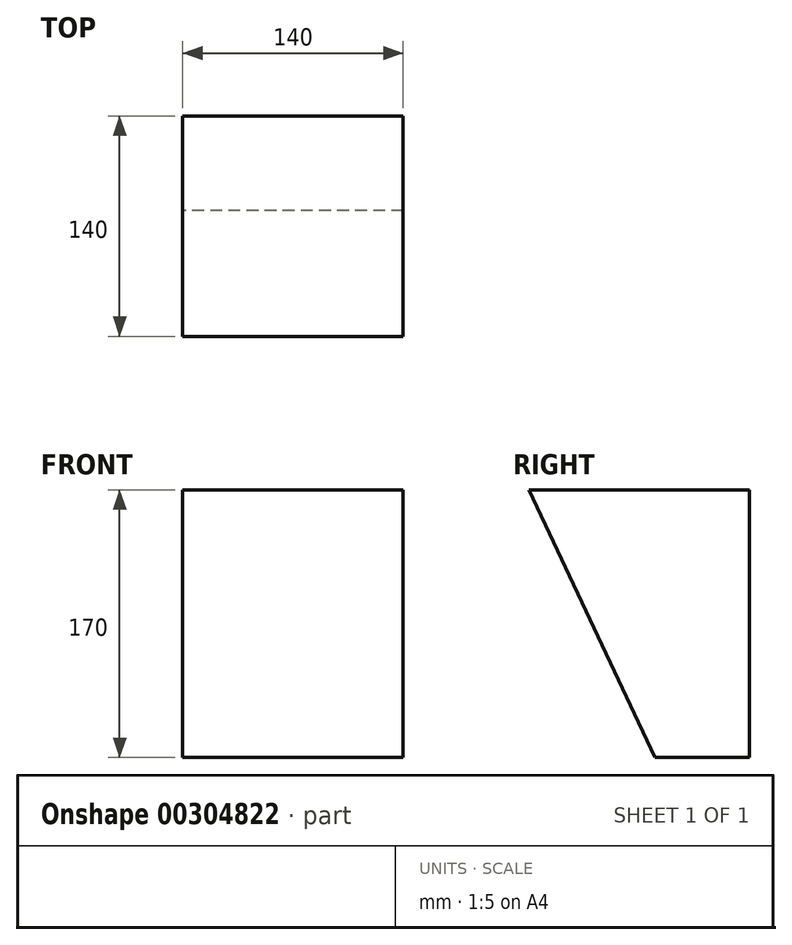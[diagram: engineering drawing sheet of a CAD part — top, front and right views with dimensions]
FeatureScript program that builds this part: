
annotation { "Feature Type Name" : "Feature", "Feature Type Description" : "" }
export const myFeature = defineFeature(function(context is Context, id is Id, definition is map)
    precondition{}
    {
        {
            var Q0;
            Q0=qCreatedBy(makeId("Top.planeOp"),FACE);
            cPlane(context, id + "F0", {"entities" : qUnion([Q0]), "cplaneType" : CPlaneType.OFFSET, "offset" : 170 * mm, "width" : 150 * mm, "height" : 150 * mm});
        }
        {
            var Q0;
            Q0=qCreatedBy(id+"F0.planeOp",FACE);
            var sketch = newSketch(context, id + "F1", { "sketchPlane" : qUnion([Q0])});
            skLineSegment(sketch, "E0.bottom", {"start": v(70, -140) * mm, "end": v(-70, -140) * mm});
            skLineSegment(sketch, "E0.top", {"start": v(70, 0) * mm, "end": v(-70, 0) * mm});
            skLineSegment(sketch, "E0.left", {"start": v(70, -140) * mm, "end": v(70, 0) * mm});
            skLineSegment(sketch, "E0.right", {"start": v(-70, -140) * mm, "end": v(-70, 0) * mm});
            skPoint(sketch, "E0.middle", {"position": v(0, 0) * mm});
            skSolve(sketch);
        }
        {
            var Q0;
            Q0=qCreatedBy(makeId("Top.planeOp"),FACE);
            var sketch = newSketch(context, id + "F2", { "sketchPlane" : qUnion([Q0])});
            skPoint(sketch, "E1", {"position": v(-340, 140) * mm});
            skPoint(sketch, "E2", {"position": v(-340, -140) * mm});
            skPoint(sketch, "E3", {"position": v(0, -60) * mm});
            skPoint(sketch, "E4", {"position": v(0, 60) * mm});
            skLineSegment(sketch, "E5", {"start": v(-340, 140) * mm, "end": v(-340, -140) * mm});
            skLineSegment(sketch, "E6", {"start": v(0, -60) * mm, "end": v(-340, -140) * mm});
            skLineSegment(sketch, "E7", {"start": v(0, 60) * mm, "end": v(0, -60) * mm});
            skLineSegment(sketch, "E8", {"start": v(0, 60) * mm, "end": v(-340, 140) * mm});
            skPoint(sketch, "E9", {"position": v(-340, 0) * mm});
            skPoint(sketch, "E10", {"position": v(0, 0) * mm});
            skPoint(sketch, "E11", {"position": v(-170, 0) * mm});
            skLineSegment(sketch, "E12", {"start": v(-170, 100) * mm, "end": v(-170, -100) * mm});
            skLineSegment(sketch, "E13", {"start": v(-170, 0) * mm, "end": v(-340, 0) * mm});
            skPoint(sketch, "E14", {"position": v(-255, 0) * mm});
            skLineSegment(sketch, "E15", {"start": v(-255, 120) * mm, "end": v(-255, -120) * mm});
            skLineSegment(sketch, "E16", {"start": v(-42.5, 70) * mm, "end": v(-42.5, -70) * mm});
            skPoint(sketch, "E17", {"position": v(-42.5, 0) * mm});
            skLineSegment(sketch, "E18", {"start": v(-100, 83.53) * mm, "end": v(-100, -83.53) * mm});
            skSolve(sketch);
        }
        {
            var Q0;
            Q0=qCreatedBy(makeId("Top.planeOp"),FACE);
            var sketch = newSketch(context, id + "F3", { "sketchPlane" : qUnion([Q0])});
            skLineSegment(sketch, "E19.bottom", {"start": v(70, -60) * mm, "end": v(-70, -60) * mm});
            skLineSegment(sketch, "E19.top", {"start": v(70, 0) * mm, "end": v(-70, 0) * mm});
            skLineSegment(sketch, "E19.left", {"start": v(70, -60) * mm, "end": v(70, 0) * mm});
            skLineSegment(sketch, "E19.right", {"start": v(-70, -60) * mm, "end": v(-70, 0) * mm});
            skPoint(sketch, "E19.middle", {"position": v(0, -30) * mm});
            skSolve(sketch);
        }
        {
            var Q0;
            Q0=qCreatedBy(makeId("Top.planeOp"),FACE);
            cPlane(context, id + "F4", {"entities" : qUnion([Q0]), "cplaneType" : CPlaneType.OFFSET, "offset" : 85 * mm, "width" : 150 * mm, "height" : 150 * mm});
        }
        {
            var Q0;
            Q0=qCreatedBy(id+"F4.planeOp",FACE);
            var sketch = newSketch(context, id + "F5", { "sketchPlane" : qUnion([Q0])});
            skLineSegment(sketch, "E20.bottom", {"start": v(70, 0) * mm, "end": v(-70, 0) * mm});
            skLineSegment(sketch, "E20.top", {"start": v(70, -100) * mm, "end": v(-70, -100) * mm});
            skLineSegment(sketch, "E20.left", {"start": v(70, 0) * mm, "end": v(70, -100) * mm});
            skLineSegment(sketch, "E20.right", {"start": v(-70, 0) * mm, "end": v(-70, -100) * mm});
            skPoint(sketch, "E20.middle", {"position": v(0, -50) * mm});
            skSolve(sketch);
        }
        {
            var Q0;
            Q0=makeQuery(id+"F1.imprint","IMPRINT",FACE,{"disambiguationData":[TD([[makeQuery(id+"F1.imprint","IMPRINT",EDGE,{"derivedFrom":sQuery(id+"F1.wireOp",EDGE,"E0.bottom")}),-1.0]])]});
            var Q1;
            Q1=makeQuery(id+"F5.imprint","IMPRINT",FACE,{"disambiguationData":[TD([[makeQuery(id+"F5.imprint","IMPRINT",EDGE,{"derivedFrom":sQuery(id+"F5.wireOp",EDGE,"E20.bottom")}),1.0]])]});
            loft(context, id + "F6", {"sheetProfilesArray" : [{ "sheetProfileEntities" : qUnion([Q0]) }, { "sheetProfileEntities" : qUnion([Q1]) }]});
        }
        {
            var Q1;
            Q1=makeQuery(id+"F6.opLoft","CAP_FACE",FACE,{"disambiguationData":[OSD([makeQuery(id+"F5.imprint","IMPRINT",FACE,{"disambiguationData":[TD([[makeQuery(id+"F5.imprint","IMPRINT",EDGE,{"derivedFrom":sQuery(id+"F5.wireOp",EDGE,"E20.bottom")}),1.0]])]})])],"isStart":true});
            var Q2;
            Q2=makeQuery(id+"F3.imprint","IMPRINT",FACE,{"disambiguationData":[TD([[makeQuery(id+"F3.imprint","IMPRINT",EDGE,{"derivedFrom":sQuery(id+"F3.wireOp",EDGE,"E19.bottom")}),-1.0]])]});
            loft(context, id + "F7", {"operationType" : NewBodyOperationType.ADD, "sheetProfilesArray" : [{ "sheetProfileEntities" : qUnion([Q1]) }, { "sheetProfileEntities" : qUnion([Q2]) }]});
        }
        {
            var Q0;
            Q0=qCreatedBy(makeId("Top.planeOp"),FACE);
            cPlane(context, id + "F8", {"entities" : qUnion([Q0]), "cplaneType" : CPlaneType.OFFSET, "offset" : 40 * mm, "oppositeDirection" : true, "width" : 150 * mm, "height" : 150 * mm});
        }
    });
